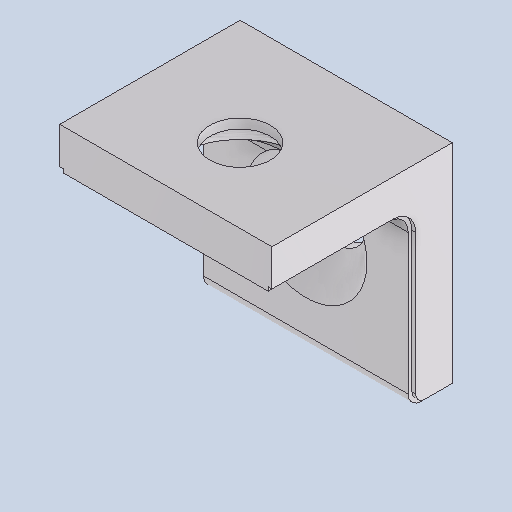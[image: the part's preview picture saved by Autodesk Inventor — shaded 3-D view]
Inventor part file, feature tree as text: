
AUTODESK INVENTOR PART (.ipt)
format: ipt  version: 2025 (Build 290162010, 162A)  size: 188,416 bytes
history: native  units: mm
features: extrude x1, sketch x1, other x1
ambient origin geometry x8: Origin, YZ Plane, XZ Plane, XY Plane, X Axis, Y Axis, Z Axis, Center Point
bodies: Volumenkörper1 (feature_tree)
feature tree (3):
  extrude  "Extrusion1"  [1 undecoded]
  sketch  "Skizze1"  dims[d0=3.0mm d1=0.0mm]
  other  "item_67777_winkel-5-20-weissalumini__high_1_1:1"
note: 1 required parameter value undecoded (feature->parameter linkage not recoverable at this tier; creation-order binding heuristic only, values carry confidence <= 0.55)
